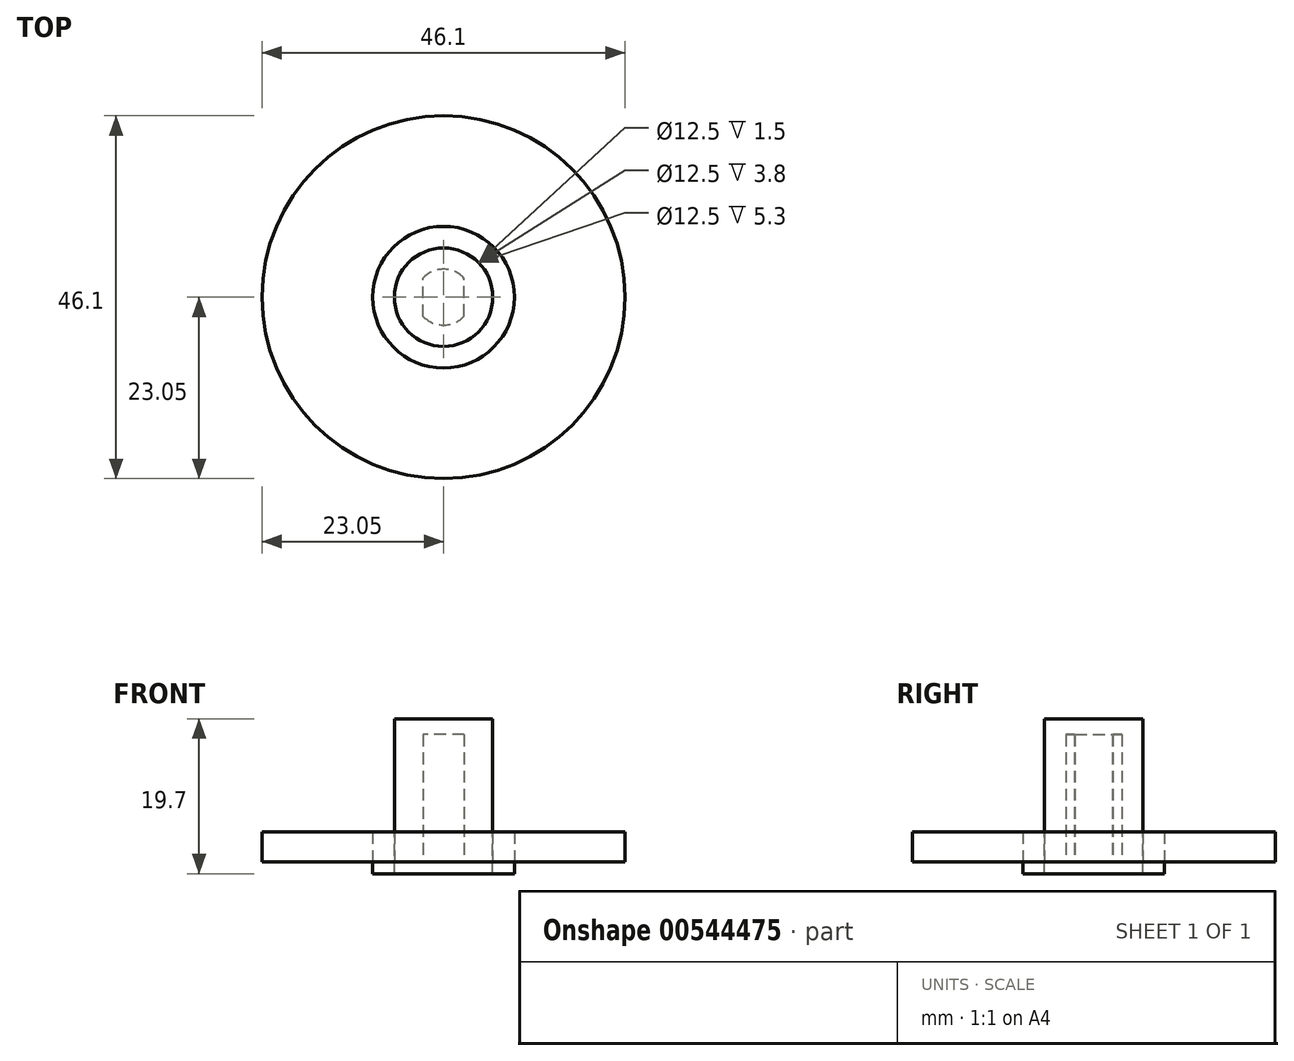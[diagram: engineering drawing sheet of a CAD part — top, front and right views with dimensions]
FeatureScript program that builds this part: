
annotation { "Feature Type Name" : "Feature", "Feature Type Description" : "" }
export const myFeature = defineFeature(function(context is Context, id is Id, definition is map)
    precondition{}
    {
        {
            var Q0;
            Q0=qCreatedBy(makeId("Top.planeOp"),FACE);
            var sketch = newSketch(context, id + "F0", { "sketchPlane" : qUnion([Q0])});
            skCircle(sketch, "E0", {"center": v(0, 0) * mm, "radius": 23.05 * mm});
            skCircle(sketch, "E1", {"center": v(0, 0) * mm, "radius": 6.25 * mm});
            skCircle(sketch, "E2", {"center": v(0, 0) * mm, "radius": 9 * mm});
            skLineSegment(sketch, "E3.left", {"start": v(-2.59, -2.43) * mm, "end": v(-2.59, 2.43) * mm});
            skLineSegment(sketch, "E3.right", {"start": v(2.62, -2.4) * mm, "end": v(2.62, 2.4) * mm});
            skArc(sketch, "E4", {"start": v(2.62, 2.4) * mm, "mid": v(0.03, 3.55) * mm, "end": v(-2.59, 2.43) * mm});
            skArc(sketch, "E5.trimOffspring", {"start": v(-2.59, -2.43) * mm, "mid": v(0.03, -3.55) * mm, "end": v(2.62, -2.4) * mm});
            skSolve(sketch);
        }
        {
            var Q0;
            Q0=makeQuery(id+"F0.imprint","IMPRINT",FACE,{"disambiguationData":[TD([[makeQuery(id+"F0.imprint","IMPRINT",EDGE,{"derivedFrom":sQuery(id+"F0.wireOp",EDGE,"E1")}),1.0]])]});
            extrude(context, id + "F1", {"entities" : qUnion([Q0]), "depth" : 16.2 * mm, "offsetDistance" : 25 * mm});
        }
        {
            var Q0;
            Q0=makeQuery(id+"F0.imprint","IMPRINT",FACE,{"disambiguationData":[TD([[makeQuery(id+"F0.imprint","IMPRINT",EDGE,{"derivedFrom":sQuery(id+"F0.wireOp",EDGE,"E0")}),1.0]])]});
            extrude(context, id + "F2", {"entities" : qUnion([Q0]), "operationType" : NewBodyOperationType.ADD, "depth" : 3.8 * mm, "offsetDistance" : 25 * mm});
        }
        {
            var Q0;
            Q0=makeQuery(id+"F0.imprint","IMPRINT",FACE,{"disambiguationData":[TD([[makeQuery(id+"F0.imprint","IMPRINT",EDGE,{"derivedFrom":sQuery(id+"F0.wireOp",EDGE,"E1")}),-1.0]])]});
            extrude(context, id + "F3", {"entities" : qUnion([Q0]), "oppositeDirection" : true, "depth" : 1.5 * mm, "offsetDistance" : 25 * mm});
        }
        {
            var Q0;
            Q0=makeQuery(id+"F0.imprint","IMPRINT",FACE,{"disambiguationData":[TD([[makeQuery(id+"F0.imprint","IMPRINT",EDGE,{"derivedFrom":sQuery(id+"F0.wireOp",EDGE,"E1")}),-1.0]])]});
            extrude(context, id + "F4", {"entities" : qUnion([Q0]), "depth" : 3.8 * mm, "offsetDistance" : 25 * mm});
        }
        {
            var Q0;
            Q0=makeQuery(id+"F1.opExtrude","CAP_FACE",FACE,{"disambiguationData":[OSD([sQuery(id+"F0.wireOp",EDGE,"E1"),sQuery(id+"F0.wireOp",EDGE,"E3.left"),sQuery(id+"F0.wireOp",EDGE,"E3.right"),sQuery(id+"F0.wireOp",EDGE,"E4"),sQuery(id+"F0.wireOp",EDGE,"E5.trimOffspring")])],"isStart":false});
            var sketch = newSketch(context, id + "F5", { "sketchPlane" : qUnion([Q0])});
            skCircle(sketch, "E6", {"center": v(0, 0) * mm, "radius": 6.25 * mm});
            skSolve(sketch);
        }
        {
            var Q0;
            Q0=makeQuery(id+"F5.imprint","IMPRINT",FACE,{"disambiguationData":[TD([[makeQuery(id+"F5.imprint","IMPRINT",EDGE,{"derivedFrom":sQuery(id+"F5.wireOp",EDGE,"E6")}),1.0]])]});
            var Q1;
            Q1=makeQuery(id+"F5.imprint","IMPRINT",FACE,{"disambiguationData":[TD([[makeQuery(id+"F5.imprint","IMPRINT",EDGE,{"derivedFrom":makeQuery(id+"F1.opExtrude","CAP_EDGE",EDGE,{"disambiguationData":[OSD([sQuery(id+"F0.wireOp",EDGE,"E3.left")])],"isStart":false})}),-1.0]])]});
            extrude(context, id + "F6", {"entities" : qUnion([Q0, Q1]), "operationType" : NewBodyOperationType.ADD, "depth" : 2 * mm, "offsetDistance" : 25 * mm});
        }
    });
